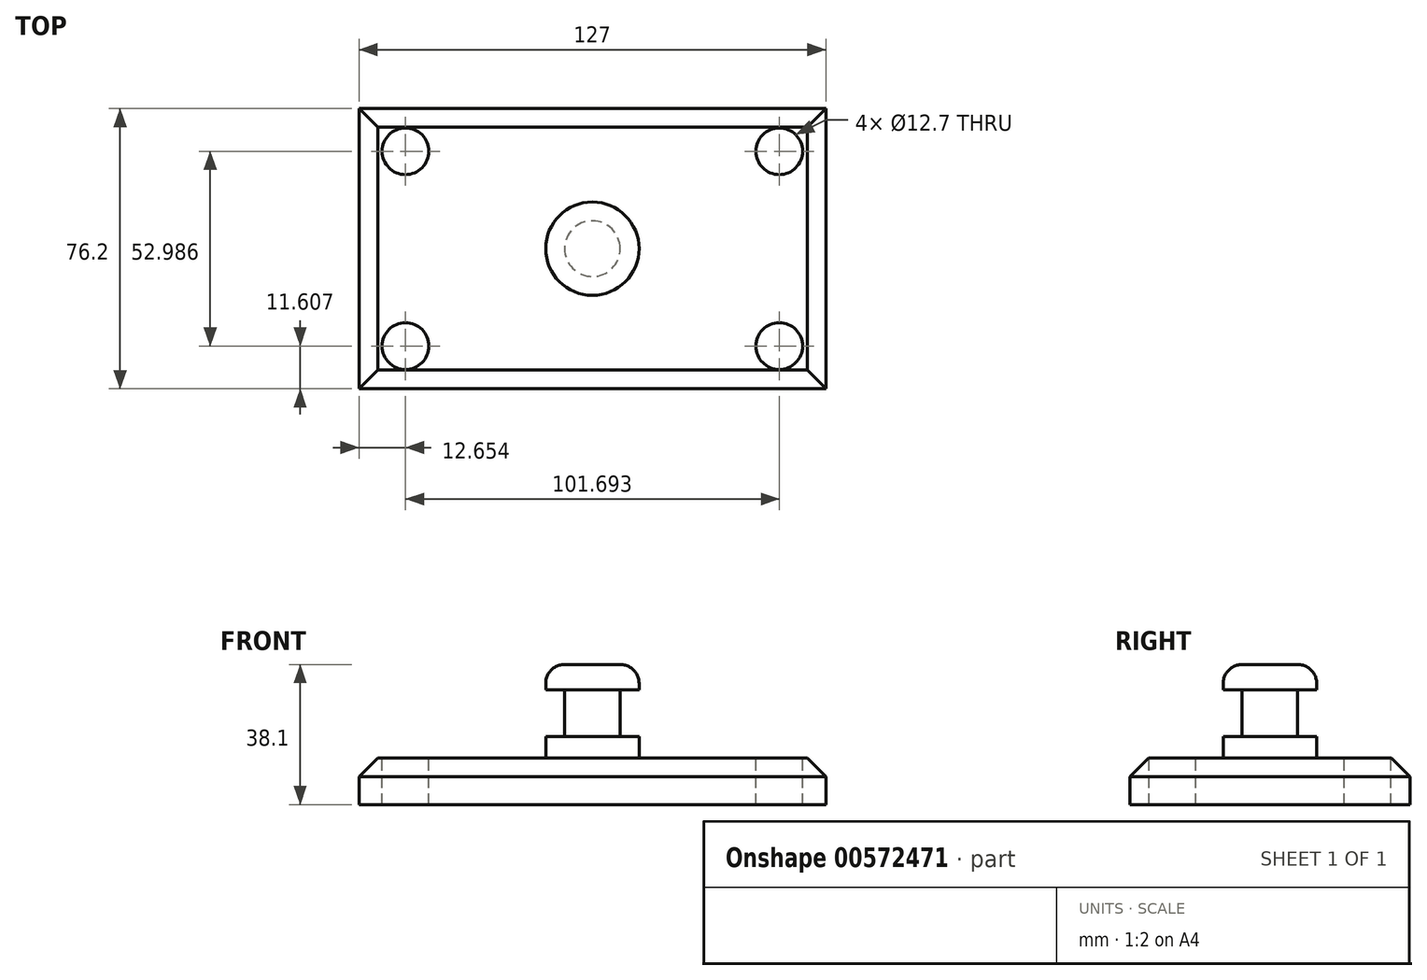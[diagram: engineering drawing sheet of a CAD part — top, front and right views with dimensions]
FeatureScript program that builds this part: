
annotation { "Feature Type Name" : "Feature", "Feature Type Description" : "" }
export const myFeature = defineFeature(function(context is Context, id is Id, definition is map)
    precondition{}
    {
        {
            var Q0;
            Q0=qCreatedBy(makeId("Top.planeOp"),FACE);
            var sketch = newSketch(context, id + "F0", { "sketchPlane" : qUnion([Q0])});
            skLineSegment(sketch, "E0.bottom", {"start": v(-63.5, 38.1) * mm, "end": v(63.5, 38.1) * mm});
            skLineSegment(sketch, "E0.top", {"start": v(-63.5, -38.1) * mm, "end": v(63.5, -38.1) * mm});
            skLineSegment(sketch, "E0.left", {"start": v(-63.5, 38.1) * mm, "end": v(-63.5, -38.1) * mm});
            skLineSegment(sketch, "E0.right", {"start": v(63.5, 38.1) * mm, "end": v(63.5, -38.1) * mm});
            skPoint(sketch, "E0.middle", {"position": v(0, 0) * mm});
            skSolve(sketch);
        }
        {
            var Q0;
            Q0=makeQuery(id+"F0.imprint","IMPRINT",FACE,{"disambiguationData":[TD([[makeQuery(id+"F0.imprint","IMPRINT",EDGE,{"derivedFrom":sQuery(id+"F0.wireOp",EDGE,"E0.bottom")}),-1.0]])]});
            extrude(context, id + "F1", {"entities" : qUnion([Q0]), "depth" : 12.7 * mm, "offsetDistance" : 25.4 * mm});
        }
        {
            var Q0;
            Q0=makeQuery(id+"F1.opExtrude","CAP_FACE",FACE,{"disambiguationData":[OSD([sQuery(id+"F0.wireOp",EDGE,"E0.bottom"),sQuery(id+"F0.wireOp",EDGE,"E0.top"),sQuery(id+"F0.wireOp",EDGE,"E0.left"),sQuery(id+"F0.wireOp",EDGE,"E0.right")])],"isStart":false});
            var sketch = newSketch(context, id + "F2", { "sketchPlane" : qUnion([Q0])});
            skLineSegment(sketch, "E1.bottom", {"start": v(-50.85, 26.5) * mm, "end": v(50.85, 26.5) * mm});
            skLineSegment(sketch, "E1.top", {"start": v(-50.85, -26.5) * mm, "end": v(50.85, -26.5) * mm});
            skLineSegment(sketch, "E1.left", {"start": v(-50.85, 26.5) * mm, "end": v(-50.85, -26.5) * mm});
            skLineSegment(sketch, "E1.right", {"start": v(50.85, 26.5) * mm, "end": v(50.85, -26.5) * mm});
            skPoint(sketch, "E1.middle", {"position": v(0, 0) * mm});
            skCircle(sketch, "E2", {"center": v(-50.85, 26.5) * mm, "radius": 6.35 * mm});
            skCircle(sketch, "E3", {"center": v(-50.85, -26.5) * mm, "radius": 6.35 * mm});
            skCircle(sketch, "E4", {"center": v(50.85, -26.5) * mm, "radius": 6.35 * mm});
            skCircle(sketch, "E5", {"center": v(50.85, 26.5) * mm, "radius": 6.35 * mm});
            skSolve(sketch);
        }
        {
            var Q0;
            {var subQ0=sQuery(id+"F2.wireOp",EDGE,"E1.left");var subQ1=sQuery(id+"F2.wireOp",EDGE,"E1.top");var subQ2=makeQuery(id+"F2.imprint","INTERSECT",VERTEX,{"derivedFrom":[subQ1,subQ0]});Q0=makeQuery(id+"F2.imprint","IMPRINT",FACE,{"disambiguationData":[TD([[makeQuery(id+"F2.imprint","IMPRINT",EDGE,{"disambiguationData":[TD([[subQ2,-1.0]])],"derivedFrom":subQ1}),-1.0]])]});}
            var Q1;
            {var subQ0=sQuery(id+"F2.wireOp",EDGE,"E1.left");var subQ1=sQuery(id+"F2.wireOp",EDGE,"E1.top");var subQ2=makeQuery(id+"F2.imprint","INTERSECT",VERTEX,{"derivedFrom":[subQ1,subQ0]});Q1=makeQuery(id+"F2.imprint","IMPRINT",FACE,{"disambiguationData":[TD([[makeQuery(id+"F2.imprint","IMPRINT",EDGE,{"disambiguationData":[TD([[subQ2,-1.0]])],"derivedFrom":subQ1}),1.0]])]});}
            var Q2;
            {var subQ0=sQuery(id+"F2.wireOp",EDGE,"E1.left");var subQ1=sQuery(id+"F2.wireOp",EDGE,"E1.bottom");var subQ2=makeQuery(id+"F2.imprint","INTERSECT",VERTEX,{"derivedFrom":[subQ1,subQ0]});Q2=makeQuery(id+"F2.imprint","IMPRINT",FACE,{"disambiguationData":[TD([[makeQuery(id+"F2.imprint","IMPRINT",EDGE,{"disambiguationData":[TD([[subQ2,-1.0]])],"derivedFrom":subQ1}),1.0]])]});}
            var Q3;
            {var subQ0=sQuery(id+"F2.wireOp",EDGE,"E1.left");var subQ1=sQuery(id+"F2.wireOp",EDGE,"E1.bottom");var subQ2=makeQuery(id+"F2.imprint","INTERSECT",VERTEX,{"derivedFrom":[subQ1,subQ0]});Q3=makeQuery(id+"F2.imprint","IMPRINT",FACE,{"disambiguationData":[TD([[makeQuery(id+"F2.imprint","IMPRINT",EDGE,{"disambiguationData":[TD([[subQ2,-1.0]])],"derivedFrom":subQ1}),-1.0]])]});}
            var Q4;
            {var subQ0=sQuery(id+"F2.wireOp",EDGE,"E1.right");var subQ1=sQuery(id+"F2.wireOp",EDGE,"E1.top");var subQ2=makeQuery(id+"F2.imprint","INTERSECT",VERTEX,{"derivedFrom":[subQ1,subQ0]});Q4=makeQuery(id+"F2.imprint","IMPRINT",FACE,{"disambiguationData":[TD([[makeQuery(id+"F2.imprint","IMPRINT",EDGE,{"disambiguationData":[TD([[subQ2,1.0]])],"derivedFrom":subQ1}),-1.0]])]});}
            var Q5;
            {var subQ0=sQuery(id+"F2.wireOp",EDGE,"E1.right");var subQ1=sQuery(id+"F2.wireOp",EDGE,"E1.top");var subQ2=makeQuery(id+"F2.imprint","INTERSECT",VERTEX,{"derivedFrom":[subQ1,subQ0]});Q5=makeQuery(id+"F2.imprint","IMPRINT",FACE,{"disambiguationData":[TD([[makeQuery(id+"F2.imprint","IMPRINT",EDGE,{"disambiguationData":[TD([[subQ2,1.0]])],"derivedFrom":subQ1}),1.0]])]});}
            var Q6;
            {var subQ0=sQuery(id+"F2.wireOp",EDGE,"E1.right");var subQ1=sQuery(id+"F2.wireOp",EDGE,"E1.bottom");var subQ2=makeQuery(id+"F2.imprint","INTERSECT",VERTEX,{"derivedFrom":[subQ1,subQ0]});Q6=makeQuery(id+"F2.imprint","IMPRINT",FACE,{"disambiguationData":[TD([[makeQuery(id+"F2.imprint","IMPRINT",EDGE,{"disambiguationData":[TD([[subQ2,1.0]])],"derivedFrom":subQ1}),1.0]])]});}
            var Q7;
            {var subQ0=sQuery(id+"F2.wireOp",EDGE,"E1.right");var subQ1=sQuery(id+"F2.wireOp",EDGE,"E1.bottom");var subQ2=makeQuery(id+"F2.imprint","INTERSECT",VERTEX,{"derivedFrom":[subQ1,subQ0]});Q7=makeQuery(id+"F2.imprint","IMPRINT",FACE,{"disambiguationData":[TD([[makeQuery(id+"F2.imprint","IMPRINT",EDGE,{"disambiguationData":[TD([[subQ2,1.0]])],"derivedFrom":subQ1}),-1.0]])]});}
            extrude(context, id + "F3", {"entities" : qUnion([Q0, Q1, Q2, Q3, Q4, Q5, Q6, Q7]), "operationType" : NewBodyOperationType.REMOVE, "endBound" : BoundingType.THROUGH_ALL, "oppositeDirection" : true, "depth" : 25.4 * mm, "offsetDistance" : 25.4 * mm});
        }
        {
            var Q0;
            Q0=qCreatedBy(makeId("Front.planeOp"),FACE);
            var sketch = newSketch(context, id + "F4", { "sketchPlane" : qUnion([Q0])});
            skLineSegment(sketch, "E6.bottom", {"start": v(0, 12.7) * mm, "end": v(12.7, 12.7) * mm});
            skLineSegment(sketch, "E6.top", {"start": v(0, 38.1) * mm, "end": v(12.7, 38.1) * mm});
            skLineSegment(sketch, "E6.left", {"start": v(0, 12.7) * mm, "end": v(0, 38.1) * mm});
            skLineSegment(sketch, "E6.right", {"start": v(12.7, 12.7) * mm, "end": v(12.7, 38.1) * mm});
            skSolve(sketch);
        }
        {
            var Q0;
            Q0=makeQuery(id+"F4.imprint","IMPRINT",FACE,{"disambiguationData":[TD([[makeQuery(id+"F4.imprint","IMPRINT",EDGE,{"derivedFrom":sQuery(id+"F4.wireOp",EDGE,"E6.bottom")}),1.0]])]});
            var Q1;
            Q1=sQuery(id+"F4.wireOp",EDGE,"E6.left");
            revolve(context, id + "F5", {"operationType" : NewBodyOperationType.ADD, "entities" : qUnion([Q0]), "axis" : qUnion([Q1]), "revolveType" : RevolveType.FULL});
        }
        {
            var Q0;
            Q0=qCreatedBy(makeId("Front.planeOp"),FACE);
            var sketch = newSketch(context, id + "F6", { "sketchPlane" : qUnion([Q0])});
            skLineSegment(sketch, "E7.bottom", {"start": v(-7.56, 31.25) * mm, "end": v(-20.26, 31.25) * mm});
            skLineSegment(sketch, "E7.top", {"start": v(-7.56, 18.55) * mm, "end": v(-20.26, 18.55) * mm});
            skLineSegment(sketch, "E7.left", {"start": v(-7.56, 31.25) * mm, "end": v(-7.56, 18.55) * mm});
            skLineSegment(sketch, "E7.right", {"start": v(-20.26, 31.25) * mm, "end": v(-20.26, 18.55) * mm});
            skSolve(sketch);
        }
        {
            var Q0;
            Q0=makeQuery(id+"F6.imprint","IMPRINT",FACE,{"disambiguationData":[TD([[makeQuery(id+"F6.imprint","IMPRINT",EDGE,{"derivedFrom":sQuery(id+"F6.wireOp",EDGE,"E7.bottom")}),1.0]])]});
            var Q1;
            Q1=makeQuery(id+"F5.opRevolve","SWEPT_FACE",FACE,{"disambiguationData":[OSD([sQuery(id+"F4.wireOp",EDGE,"E6.right")])]});
            revolve(context, id + "F7", {"operationType" : NewBodyOperationType.REMOVE, "entities" : qUnion([Q0]), "axis" : qUnion([Q1]), "revolveType" : RevolveType.FULL, "oppositeDirection" : true});
        }
        {
            var Q0;
            Q0=makeQuery(id+"F1.opExtrude","CAP_EDGE",EDGE,{"disambiguationData":[OSD([sQuery(id+"F0.wireOp",EDGE,"E0.bottom")])],"isStart":false});
            var Q1;
            Q1=makeQuery(id+"F1.opExtrude","CAP_EDGE",EDGE,{"disambiguationData":[OSD([sQuery(id+"F0.wireOp",EDGE,"E0.left")])],"isStart":false});
            var Q2;
            Q2=makeQuery(id+"F1.opExtrude","CAP_EDGE",EDGE,{"disambiguationData":[OSD([sQuery(id+"F0.wireOp",EDGE,"E0.top")])],"isStart":false});
            var Q3;
            Q3=makeQuery(id+"F1.opExtrude","CAP_EDGE",EDGE,{"disambiguationData":[OSD([sQuery(id+"F0.wireOp",EDGE,"E0.right")])],"isStart":false});
            chamfer(context, id + "F8", {"entities" : qUnion([Q0, Q1, Q2, Q3]), "width" : 5.08 * mm, "tangentPropagation" : true});
        }
        {
            var Q0;
            Q0=makeQuery(id+"F5.opRevolve","SWEPT_EDGE",EDGE,{"disambiguationData":[OSD([sQuery(id+"F4.wireOp",EDGE,"E6.top"),sQuery(id+"F4.wireOp",EDGE,"E6.right")])]});
            var Q1;
            Q1=makeQuery(id+"F5.opRevolve","SWEPT_EDGE",EDGE,{"disambiguationData":[OSD([sQuery(id+"F4.wireOp",EDGE,"E6.bottom"),sQuery(id+"F4.wireOp",EDGE,"E6.right")])]});
            fillet(context, id + "F9", {"entities" : qUnion([Q0, Q1]), "radius" : 5.08 * mm, "tangentPropagation" : true, "allowEdgeOverflow" : false});
        }
    });
